# Revit family: 11_CMP_FD312_F1A+SPL
name_source: partatom
category: Finestre
units: mm (PartAtom-declared; Revit-internal decimal feet)

## family parameters
Condiviso = Sì
Host = Muro
Numero OmniClass = 23.30.20.00
Punto di calcolo locali = Sì
Sempre verticale = Sì
Taglio con vuoti quando caricato = No
Titolo OmniClass = Windows

## types (3) — shared parameters
Altezza = 1500 mm  [stored 4.92126 ft]
Chiusura muro = Per host
Codice assieme = B2020100
Coefficiente di scambio termico (U) = 1 W/(m²·K)
Costruzione analitica = <Nessuno>
EXTERNAL ALUMINUM FRAME/TELAIO ALLUMINIO ESTERNO = UNIFORM_ALUMINUM
H = 1500 mm  [stored 4.92126 ft]
HANDLE HEIGHT/ALTEZZA MANIGLIA = 800 mm  [stored 2.62467 ft]
HANDLE/MANIGLIA = UNIFORM_ALUMINUM
HOLE_H = 1500 mm  [stored 4.92126 ft]
HOLE_W = 1000 mm  [stored 3.28084 ft]
H_FIX = 500 mm  [stored 1.64042 ft]
H_MOBILE = 1000 mm  [stored 3.28084 ft]
INTERIOR WOOD FRAME/TELAIO LEGNO INTERNO = UNIFORM_WOOD
Immagine tipo = <Nessuno>
Larghezza = 1000 mm  [stored 3.28084 ft]
MAXIMUM WIDTH/LARGHEZZA MASSIMA = 1200 mm
MAX_DIMENSIONS_WARNING = No
MINIMUM WIDTH/LARGHEZZA MINIMA  = 400 mm  [stored 1.31234 ft]
Modello = COMPLANARE
PRODUCER WEBSITE/SITO WEB PRODUTTORE = www.uniform.it
PRODUCT WEBSITE/SITO WEB PRODOTTO = www.sistema-uni-one.it
Produttore = UNIFORM
URL = https://www.sistema-uni-one.it
W = 1000 mm  [stored 3.28084 ft]
WINDOW GLASS/VETRO FINESTRA = UNIFORM_GLASS
WINDOW SILL/BANCALINO FINESTRA = UNIFORM_STONE
zero-valued in all types: Indice di riscaldamento alla radiazione solare, T_F_H, Trasmittanza luminosa, WINDOW HOLE TOLERANCE/TOLLERANZA FORO FINESTRA

## per-type parameters (varying)
| type | Altezza di default del davanzale | GLASS WEIGHT/PESO VETRO | MAXIMUM HEIGHT/ALTEZZA MASSIMA | MINIMUM HEIGHT/ALTEZZA MINIMA | Resistenza termica (R) | Rw GLASS/Rw VETRO | Rw WINDOW/Rw FINESTRA | Ug GLASS/Ug VETRO | Uw WINDOW/Uw FINESTRA |
| F1A+SPL_ACOUSTICS | 600 mm | 60.00 kg/m² | 2800 mm  [stored 9.18635 ft] | 800 mm  [stored 2.62467 ft] | 0.0000 (m²·K)/W | 49 | 43 | 1.1 W/(m²·K) | 1.3 W/(m²·K) |
| F1A+SPL_THERMAL | 800 mm  [stored 2.62467 ft] | 43.00 kg/m² | 2000 mm  [stored 6.56168 ft] | 400 mm  [stored 1.31234 ft] | 1.7611 (m²·K)/W | 0 | 0 | 1 W/(m²·K) | 1.2 W/(m²·K) |
| F1A+SPL_HIGH THERMAL PERFORMANCE | 800 mm  [stored 2.62467 ft] | 43.00 kg/m² | 2800 mm  [stored 9.18635 ft] | 800 mm  [stored 2.62467 ft] | 0.0000 (m²·K)/W | 0 | 0 | 0.5 W/(m²·K) | 0.8 W/(m²·K) |

note: [stored X ft] marks values corroborated as IEEE doubles in the binary element streams (Revit-internal decimal feet)
